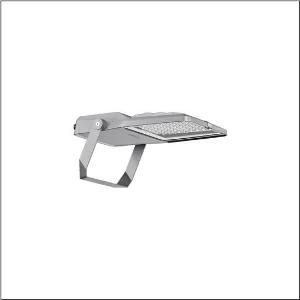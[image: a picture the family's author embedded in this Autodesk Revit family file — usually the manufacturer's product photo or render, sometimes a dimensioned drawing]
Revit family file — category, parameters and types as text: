
# Revit family: floodlight_fl_21_iq_mini___pl52_5xa7772b4d1a_9164
name_source: partatom
category: Lighting Fixtures
units: mm (PartAtom-declared; Revit-internal decimal feet)

## family parameters
Cut with Voids When Loaded = No
Host = Face
Light Source = No
Part Type = Normal
Room Calculation Point = No
Round Connector Dimension = Use Diameter
Shared = No

## types (1)
- --- (1 x LED, 6490 lm, 45.5 W, 4000K)
    Apparent Load = 46 VA
    CIE Flux Codes = 26 60 98 100 100
    Color Rendering = 70
    Color Temperature = 4000K
    Default Elevation = 1800 mm
    Description = Floodlight FL 21 iQ mini, floodlight, primary light control with lens, of PMMA, primary optical cover: protective disc, of toughened safety glass, transparent, light distribution: PL52, light emission: direct distribution, installation type: surface-mounted, LED, High Power LED, rated luminous flux: 6.490lm, luminous efficacy: 143lm/W, light colour: 740, colour temperature: 4000K, control: Street-Remote, Auto-Match, Temp-Guard, Night-Set, Smart-Wire, Desk-Remote (wireless, voltage-free reading and setting of iQ features in the workshop via application-optimized NFC function/RFID function), optimised constant luminous flux control (CLO 2.0), with terminal, 6-pole, mains connection: 220..240V, AC, 50/60Hz, start of lifetime: 46W, end of service life: 48W, reduction: 22W, luminaire housing, of diecast aluminium, powder-coated, Siteco® metallic grey (DB 702S), corrosivity category C5 mid according to DIN EN ISO 12944, sealing non-destructively replaceable, mounting bracket, of steel, galvanised, powder-coated, Siteco® metallic grey (DB 702S), protection rating (complete): IP66, insulation class (complete): insulation class II (safety insulation), certification: CE, ENEC, VDE, protection symbol: D, impact resistance: IK08, permissible operating ambient temperature: -40..+40°C, permissible operating ambient temperature for outdoor applications: -40..+50°C, standard: DIN EN 12944, LABS conformity tested according to VDMA 24364:2018-05, packaging unit: 1 piece

Light Distribution: PL52
    Height = 70 mm
    Lamp = 1 x LED
    Lamp Light Flux = 6490 lm
    Lamp Power = 45.5 W
    Lamp count = 1
    Length = 485 mm
    Luminous efficacy = 143 lm/W
    Manufacturer = Siteco
    ModVariant = No
    Model = 5XA7772B4D1A
    Number of Poles = 1
    OnlyDefault = Yes
    Power Factor = 1
    Product Name = Floodlight FL 21 iQ mini | PL52
    Product group = floodlight | pylon annexe
    ProductGroupID = 6200
    Protection Class = Protection class II
    Protection Degree = IP 66
    RLX_Detail_Level = 1
    RLX_Emergency_Light_Flux = 0 lm
    RLX_Emergency_Type = 0
    RLX_Emergency_Type_DB = No
    RlxData = <blob elided: 96293 chars, md5=bd41d337>
    Socket = socket
    Standby Power = 0 W
    System Light Flux = 6490 lm
    System Power = 46 W
    Type Comments = factory setting: luminous flux: 100 % | dim-lin: 254 | 463 mA
    Type Image = l_1006845.jpg
    URL = http://relux.com
    VarID = @adj_114923
    Voltage = 0 V
    Weight = 0.00 kg
    Width = 337 mm

## geometry (parser evidence)
native form markers: Blend x4, Sweep x16
no freeform markers — native parametric forms only
